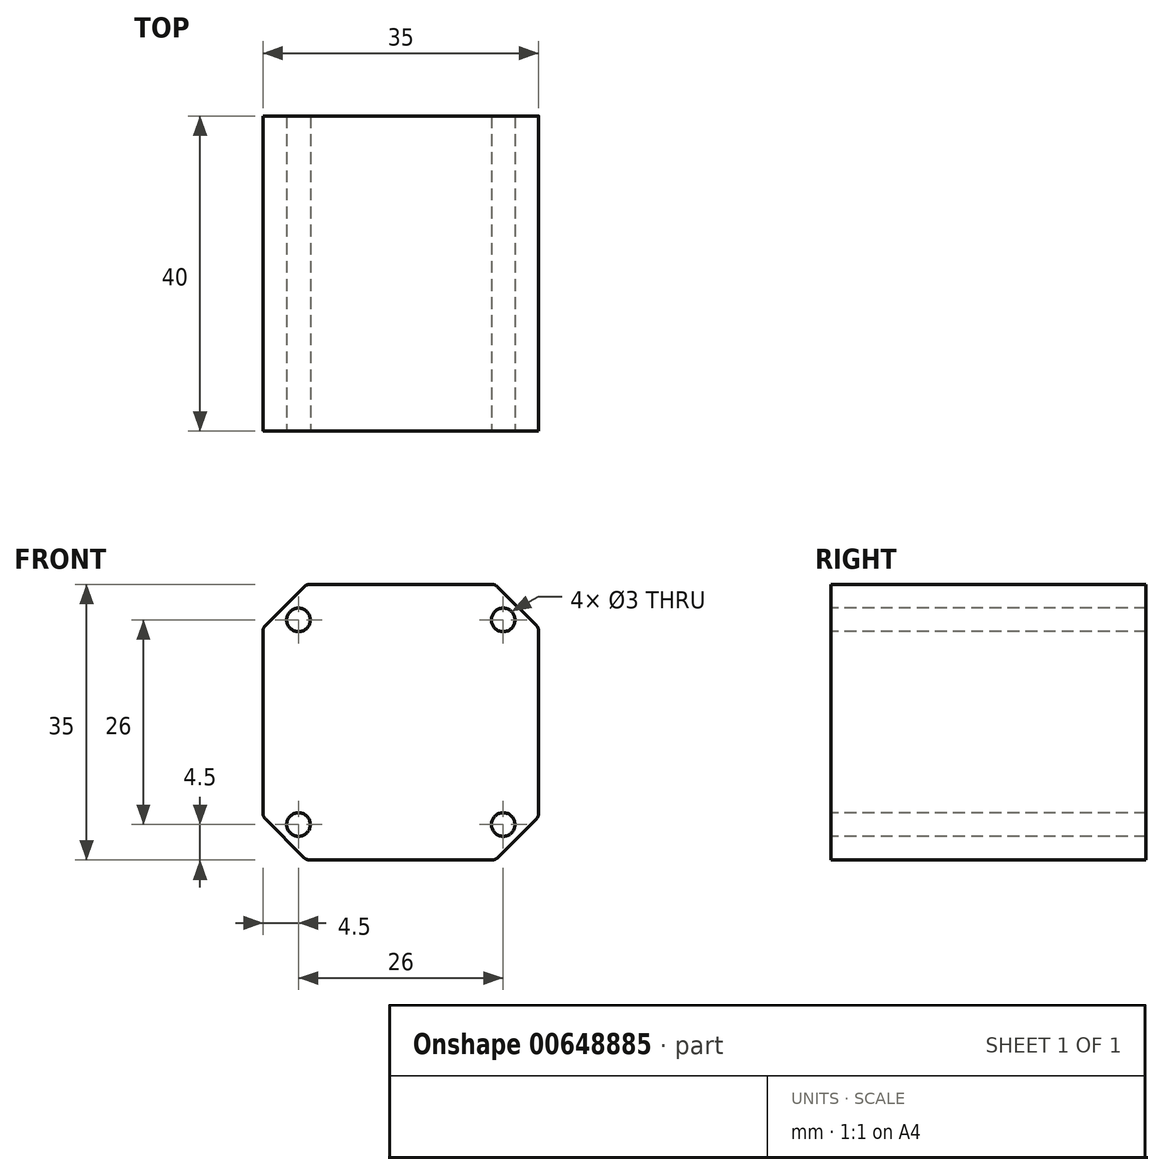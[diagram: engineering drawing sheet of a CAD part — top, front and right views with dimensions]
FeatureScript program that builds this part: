
annotation { "Feature Type Name" : "Feature", "Feature Type Description" : "" }
export const myFeature = defineFeature(function(context is Context, id is Id, definition is map)
    precondition{}
    {
        {
            var Q0;
            Q0=qCreatedBy(makeId("Front.planeOp"),FACE);
            var sketch = newSketch(context, id + "F0", { "sketchPlane" : qUnion([Q0])});
            skLineSegment(sketch, "E0.bottom", {"start": v(-17.5, 17.5) * mm, "end": v(17.5, 17.5) * mm});
            skLineSegment(sketch, "E0.top", {"start": v(-17.5, -17.5) * mm, "end": v(17.5, -17.5) * mm});
            skLineSegment(sketch, "E0.left", {"start": v(-17.5, 17.5) * mm, "end": v(-17.5, -17.5) * mm});
            skLineSegment(sketch, "E0.right", {"start": v(17.5, 17.5) * mm, "end": v(17.5, -17.5) * mm});
            skPoint(sketch, "E0.middle", {"position": v(0, 0) * mm});
            skSolve(sketch);
        }
        {
            var Q0;
            Q0 = qSketchRegion(id + "F0", true);
            extrude(context, id + "F1", {"entities" : qUnion([Q0]), "depth" : 40 * mm, "offsetDistance" : 25 * mm});
        }
        {
            var Q0;
            Q0=makeQuery(id+"F1.opExtrude","SWEPT_EDGE",EDGE,{"disambiguationData":[OSD([sQuery(id+"F0.wireOp",EDGE,"E0.bottom"),sQuery(id+"F0.wireOp",EDGE,"E0.right")])]});
            var Q1;
            Q1=makeQuery(id+"F1.opExtrude","SWEPT_EDGE",EDGE,{"disambiguationData":[OSD([sQuery(id+"F0.wireOp",EDGE,"E0.bottom"),sQuery(id+"F0.wireOp",EDGE,"E0.left")])]});
            var Q2;
            Q2=makeQuery(id+"F1.opExtrude","SWEPT_EDGE",EDGE,{"disambiguationData":[OSD([sQuery(id+"F0.wireOp",EDGE,"E0.top"),sQuery(id+"F0.wireOp",EDGE,"E0.left")])]});
            var Q3;
            Q3=makeQuery(id+"F1.opExtrude","SWEPT_EDGE",EDGE,{"disambiguationData":[OSD([sQuery(id+"F0.wireOp",EDGE,"E0.top"),sQuery(id+"F0.wireOp",EDGE,"E0.right")])]});
            chamfer(context, id + "F2", {"entities" : qUnion([Q0, Q1, Q2, Q3]), "width" : 5.5 * mm, "tangentPropagation" : true});
        }
        {
            var Q0;
            {var subQ0=sQuery(id+"F0.wireOp",EDGE,"E0.bottom");Q0=makeQuery(id+"F2.opChamfer","BLEND_EDGE",EDGE,{"blendedFrom":[makeQuery(id+"F1.opExtrude","SWEPT_EDGE",EDGE,{"disambiguationData":[OSD([subQ0,sQuery(id+"F0.wireOp",EDGE,"E0.left")])]}),makeQuery(id+"F1.opExtrude","SWEPT_FACE",FACE,{"disambiguationData":[OSD([subQ0])]})],"blendedInto":[makeQuery(id+"F1.opExtrude","SWEPT_FACE",FACE,{"disambiguationData":[OSD([subQ0])]})]});}
            var Q1;
            {var subQ0=sQuery(id+"F0.wireOp",EDGE,"E0.bottom");Q1=makeQuery(id+"F2.opChamfer","BLEND_EDGE",EDGE,{"blendedFrom":[makeQuery(id+"F1.opExtrude","SWEPT_EDGE",EDGE,{"disambiguationData":[OSD([subQ0,sQuery(id+"F0.wireOp",EDGE,"E0.right")])]}),makeQuery(id+"F1.opExtrude","SWEPT_FACE",FACE,{"disambiguationData":[OSD([subQ0])]})],"blendedInto":[makeQuery(id+"F1.opExtrude","SWEPT_FACE",FACE,{"disambiguationData":[OSD([subQ0])]})]});}
            var Q2;
            {var subQ0=sQuery(id+"F0.wireOp",EDGE,"E0.right");Q2=makeQuery(id+"F2.opChamfer","BLEND_EDGE",EDGE,{"blendedFrom":[makeQuery(id+"F1.opExtrude","SWEPT_EDGE",EDGE,{"disambiguationData":[OSD([sQuery(id+"F0.wireOp",EDGE,"E0.bottom"),subQ0])]}),makeQuery(id+"F1.opExtrude","SWEPT_FACE",FACE,{"disambiguationData":[OSD([subQ0])]})],"blendedInto":[makeQuery(id+"F1.opExtrude","SWEPT_FACE",FACE,{"disambiguationData":[OSD([subQ0])]})]});}
            var Q3;
            {var subQ0=sQuery(id+"F0.wireOp",EDGE,"E0.right");Q3=makeQuery(id+"F2.opChamfer","BLEND_EDGE",EDGE,{"blendedFrom":[makeQuery(id+"F1.opExtrude","SWEPT_EDGE",EDGE,{"disambiguationData":[OSD([sQuery(id+"F0.wireOp",EDGE,"E0.top"),subQ0])]}),makeQuery(id+"F1.opExtrude","SWEPT_FACE",FACE,{"disambiguationData":[OSD([subQ0])]})],"blendedInto":[makeQuery(id+"F1.opExtrude","SWEPT_FACE",FACE,{"disambiguationData":[OSD([subQ0])]})]});}
            var Q4;
            {var subQ0=sQuery(id+"F0.wireOp",EDGE,"E0.top");Q4=makeQuery(id+"F2.opChamfer","BLEND_EDGE",EDGE,{"blendedFrom":[makeQuery(id+"F1.opExtrude","SWEPT_EDGE",EDGE,{"disambiguationData":[OSD([subQ0,sQuery(id+"F0.wireOp",EDGE,"E0.right")])]}),makeQuery(id+"F1.opExtrude","SWEPT_FACE",FACE,{"disambiguationData":[OSD([subQ0])]})],"blendedInto":[makeQuery(id+"F1.opExtrude","SWEPT_FACE",FACE,{"disambiguationData":[OSD([subQ0])]})]});}
            var Q5;
            {var subQ0=sQuery(id+"F0.wireOp",EDGE,"E0.left");Q5=makeQuery(id+"F2.opChamfer","BLEND_EDGE",EDGE,{"blendedFrom":[makeQuery(id+"F1.opExtrude","SWEPT_EDGE",EDGE,{"disambiguationData":[OSD([sQuery(id+"F0.wireOp",EDGE,"E0.top"),subQ0])]}),makeQuery(id+"F1.opExtrude","SWEPT_FACE",FACE,{"disambiguationData":[OSD([subQ0])]})],"blendedInto":[makeQuery(id+"F1.opExtrude","SWEPT_FACE",FACE,{"disambiguationData":[OSD([subQ0])]})]});}
            var Q6;
            {var subQ0=sQuery(id+"F0.wireOp",EDGE,"E0.top");Q6=makeQuery(id+"F2.opChamfer","BLEND_EDGE",EDGE,{"blendedFrom":[makeQuery(id+"F1.opExtrude","SWEPT_EDGE",EDGE,{"disambiguationData":[OSD([subQ0,sQuery(id+"F0.wireOp",EDGE,"E0.left")])]}),makeQuery(id+"F1.opExtrude","SWEPT_FACE",FACE,{"disambiguationData":[OSD([subQ0])]})],"blendedInto":[makeQuery(id+"F1.opExtrude","SWEPT_FACE",FACE,{"disambiguationData":[OSD([subQ0])]})]});}
            var Q7;
            {var subQ0=sQuery(id+"F0.wireOp",EDGE,"E0.left");Q7=makeQuery(id+"F2.opChamfer","BLEND_EDGE",EDGE,{"blendedFrom":[makeQuery(id+"F1.opExtrude","SWEPT_EDGE",EDGE,{"disambiguationData":[OSD([sQuery(id+"F0.wireOp",EDGE,"E0.bottom"),subQ0])]}),makeQuery(id+"F1.opExtrude","SWEPT_FACE",FACE,{"disambiguationData":[OSD([subQ0])]})],"blendedInto":[makeQuery(id+"F1.opExtrude","SWEPT_FACE",FACE,{"disambiguationData":[OSD([subQ0])]})]});}
            fillet(context, id + "F3", {"entities" : qUnion([Q0, Q1, Q2, Q3, Q4, Q5, Q6, Q7]), "radius" : 1 * mm, "tangentPropagation" : true, "allowEdgeOverflow" : false});
        }
        {
            var Q0;
            Q0=makeQuery(id+"F1.opExtrude","CAP_FACE",FACE,{"disambiguationData":[OSD([sQuery(id+"F0.wireOp",EDGE,"E0.bottom"),sQuery(id+"F0.wireOp",EDGE,"E0.top"),sQuery(id+"F0.wireOp",EDGE,"E0.left"),sQuery(id+"F0.wireOp",EDGE,"E0.right")])],"isStart":false});
            var sketch = newSketch(context, id + "F4", { "sketchPlane" : qUnion([Q0])});
            skCircle(sketch, "E1", {"center": v(-13, 13) * mm, "radius": 1.5 * mm});
            skCircle(sketch, "E2.1.0", {"center": v(-13, -13) * mm, "radius": 1.5 * mm});
            skCircle(sketch, "E2.2.0", {"center": v(13, -13) * mm, "radius": 1.5 * mm});
            skCircle(sketch, "E2.3.0", {"center": v(13, 13) * mm, "radius": 1.5 * mm});
            skPoint(sketch, "E2.center", {"position": v(0, 0) * mm});
            skSolve(sketch);
        }
        {
            var Q0;
            Q0 = qSketchRegion(id + "F4", true);
            extrude(context, id + "F5", {"entities" : qUnion([Q0]), "operationType" : NewBodyOperationType.REMOVE, "endBound" : BoundingType.THROUGH_ALL, "oppositeDirection" : true, "depth" : 25 * mm, "offsetDistance" : 25 * mm});
        }
    });
